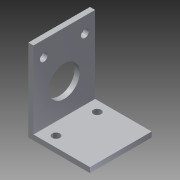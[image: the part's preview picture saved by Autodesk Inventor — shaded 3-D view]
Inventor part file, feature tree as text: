
AUTODESK INVENTOR PART (.ipt)
format: ipt  version: 2013 (Build 170138000, 138)  size: 108,544 bytes
history: native  units: in
note: dims shown in document units (in); Inventor stores cm internally (conversion verified against a paired STEP export)
features: extrude x3, sketch x3
ambient origin geometry x8: Origin, YZ Plane, XZ Plane, XY Plane, X Axis, Y Axis, Z Axis, Center Point
bodies: Solid1 (feature_tree)
feature tree (6):
  extrude  "Extrusion1"  Depth=2.0in
  extrude  "Extrusion2"  Depth=1.5in TaperAngle=0.0deg
  extrude  "Extrusion3"  Depth=0.375in
  sketch  "Sketch1"  dims[d0=1.5in d1=2.0in]
  sketch  "Sketch2"  dims[d2=0.125in d3=1.5in d4=0.0in]
  sketch  "Sketch3"  dims[d5=1.0in d6=0.375in d7=0.1875in d8=0.1875in d9=1.5in d10=0.0in d11=0.75in d12=0.875in d13=1.0in d17=0.1875in d18=0.425in d19=1.0in d20=0.0in]
